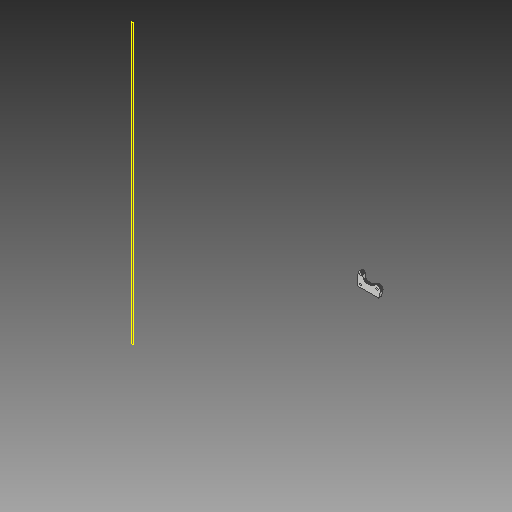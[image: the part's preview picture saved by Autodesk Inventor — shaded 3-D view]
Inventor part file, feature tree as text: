
AUTODESK INVENTOR PART (.ipt)
format: ipt  version: 2017 (Build 210142000, 142)  size: 411,136 bytes
history: native  units: mm
features: other x3, sketch x2, plane x1, extrude x1, hole x1
ambient origin geometry x8: Origin, YZ Plane, XZ Plane, XY Plane, X Axis, Y Axis, Z Axis, Center Point
bodies: Solid1 (feature_tree)
feature tree (8):
  plane  "Work Plane1"
  extrude  "Extrusion1"  [1 undecoded]
  hole  "Hole1"  [1 undecoded]
  sketch  "Sketch1"  dims[d0=6.0mm d1=0.0mm]
  sketch  "Sketch2"  dims[d2=5.2mm d3=6.0mm d4=4.0mm d5=2.0mm d6=90.0deg d7=8.0mm d8=20.594885mm]
  other  "<userpath>\OneDrive\SL-Inventor\SL-Beast 3D Printer\x-aXIS-aSSEMBLY.iam"
  other  "x-aXIS-aSSEMBLY.iam"
  other  "Makerslide 580mm:1"
note: 2 required parameter values undecoded (feature->parameter linkage not recoverable at this tier; creation-order binding heuristic only, values carry confidence <= 0.55)
